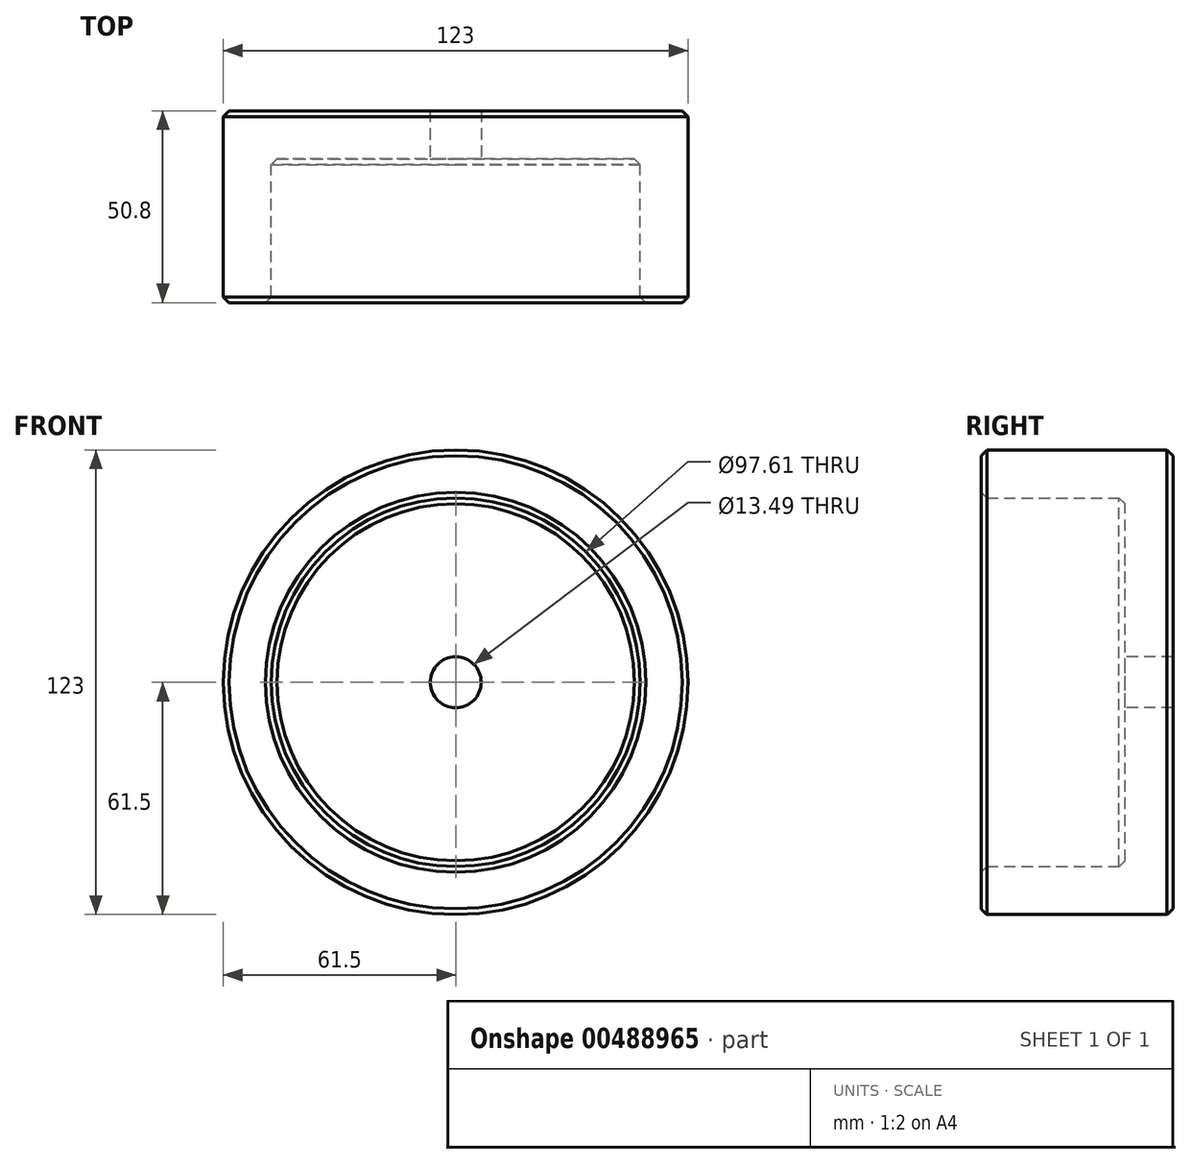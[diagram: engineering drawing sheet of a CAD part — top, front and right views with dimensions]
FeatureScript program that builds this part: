
annotation { "Feature Type Name" : "Feature", "Feature Type Description" : "" }
export const myFeature = defineFeature(function(context is Context, id is Id, definition is map)
    precondition{}
    {
        {
            var Q0;
            Q0=qCreatedBy(makeId("Front.planeOp"),FACE);
            var sketch = newSketch(context, id + "F0", { "sketchPlane" : qUnion([Q0])});
            skCircle(sketch, "E0", {"center": v(0, 0) * mm, "radius": 61.5 * mm});
            skCircle(sketch, "E1", {"center": v(0, 0) * mm, "radius": 48.8 * mm});
            skSolve(sketch);
        }
        {
            var Q0;
            Q0=makeQuery(id+"F0.imprint","IMPRINT",FACE,{"disambiguationData":[TD([[makeQuery(id+"F0.imprint","IMPRINT",EDGE,{"derivedFrom":sQuery(id+"F0.wireOp",EDGE,"E0")}),1.0]])]});
            extrude(context, id + "F1", {"entities" : qUnion([Q0]), "depth" : 38.1 * mm});
        }
        {
            var Q0;
            Q0=makeQuery(id+"F0.imprint","IMPRINT",FACE,{"disambiguationData":[TD([[makeQuery(id+"F0.imprint","IMPRINT",EDGE,{"derivedFrom":sQuery(id+"F0.wireOp",EDGE,"E0")}),1.0]])]});
            var Q1;
            Q1=makeQuery(id+"F0.imprint","IMPRINT",FACE,{"disambiguationData":[TD([[makeQuery(id+"F0.imprint","IMPRINT",EDGE,{"derivedFrom":sQuery(id+"F0.wireOp",EDGE,"E1")}),1.0]])]});
            extrude(context, id + "F2", {"entities" : qUnion([Q0, Q1]), "operationType" : NewBodyOperationType.ADD, "oppositeDirection" : true, "depth" : 12.7 * mm});
        }
        {
            var Q0;
            Q0=sQuery(id+"F0.wireOp",VERTEX,"E0.center");
            var Q1;
            Q1=makeQuery(id+"F1.opExtrude","SWEPT_BODY",BODY,{"disambiguationData":[OSD([sQuery(id+"F0.wireOp",EDGE,"E0"),sQuery(id+"F0.wireOp",EDGE,"E1")])]});
            hole(context, id + "F3", {"style" : HoleStyle.SIMPLE, "endStyle" : HoleEndStyle.BLIND, "standardTappedOrClearance" : lookupTablePath({ "standard" : "ANSI", "fit" : "Normal (ASME)", "size" : "1/2", "type" : "Clearance" }), "standardBlindInLast" : lookupTablePath({ "fit" : "Free", "standard" : "ANSI", "size" : "1/2", "type" : "Clearance" }), "holeDiameter" : 13.5 * mm, "holeDepth" : 31.27 * mm, "tappedDepth" : 25.4 * mm, "tapClearance" : 3, "startFromSketch" : true, "locations" : qUnion([Q0]), "scope" : qUnion([Q1])});
        }
        {
            var Q0;
            {var subQ0=sQuery(id+"F0.wireOp",EDGE,"E0");Q0=makeQuery(id+"F2.boolean.opBoolean","MERGE",FACE,{"derivedFrom":[makeQuery(id+"F1.opExtrude","SWEPT_FACE",FACE,{"disambiguationData":[OSD([subQ0])]}),makeQuery(id+"F2.opExtrude","SWEPT_FACE",FACE,{"disambiguationData":[OSD([subQ0])]})]});}
            var Q1;
            Q1=makeQuery(id+"F1.opExtrude","SWEPT_FACE",FACE,{"disambiguationData":[OSD([sQuery(id+"F0.wireOp",EDGE,"E1")])]});
            chamfer(context, id + "F4", {"entities" : qUnion([Q0, Q1]), "width" : 1.52 * mm, "tangentPropagation" : true});
        }
    });
